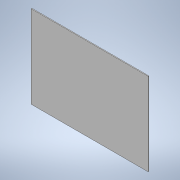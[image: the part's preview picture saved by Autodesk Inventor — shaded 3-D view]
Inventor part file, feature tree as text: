
AUTODESK INVENTOR PART (.ipt)
format: ipt  version: 2021 (Build 250183000, 183)  size: 87,552 bytes
history: native  units: mm
features: extrude x1, sketch x1
ambient origin geometry x8: Origin, YZ Plane, XZ Plane, XY Plane, X Axis, Y Axis, Z Axis, Center Point
bodies: Solid1 (feature_tree)
feature tree (2):
  extrude  "Extrusion1"  Depth=297.0mm
  sketch  "Sketch1"  dims[d0=210.0mm d1=297.0mm d2=2.0mm d3=0.0mm]
